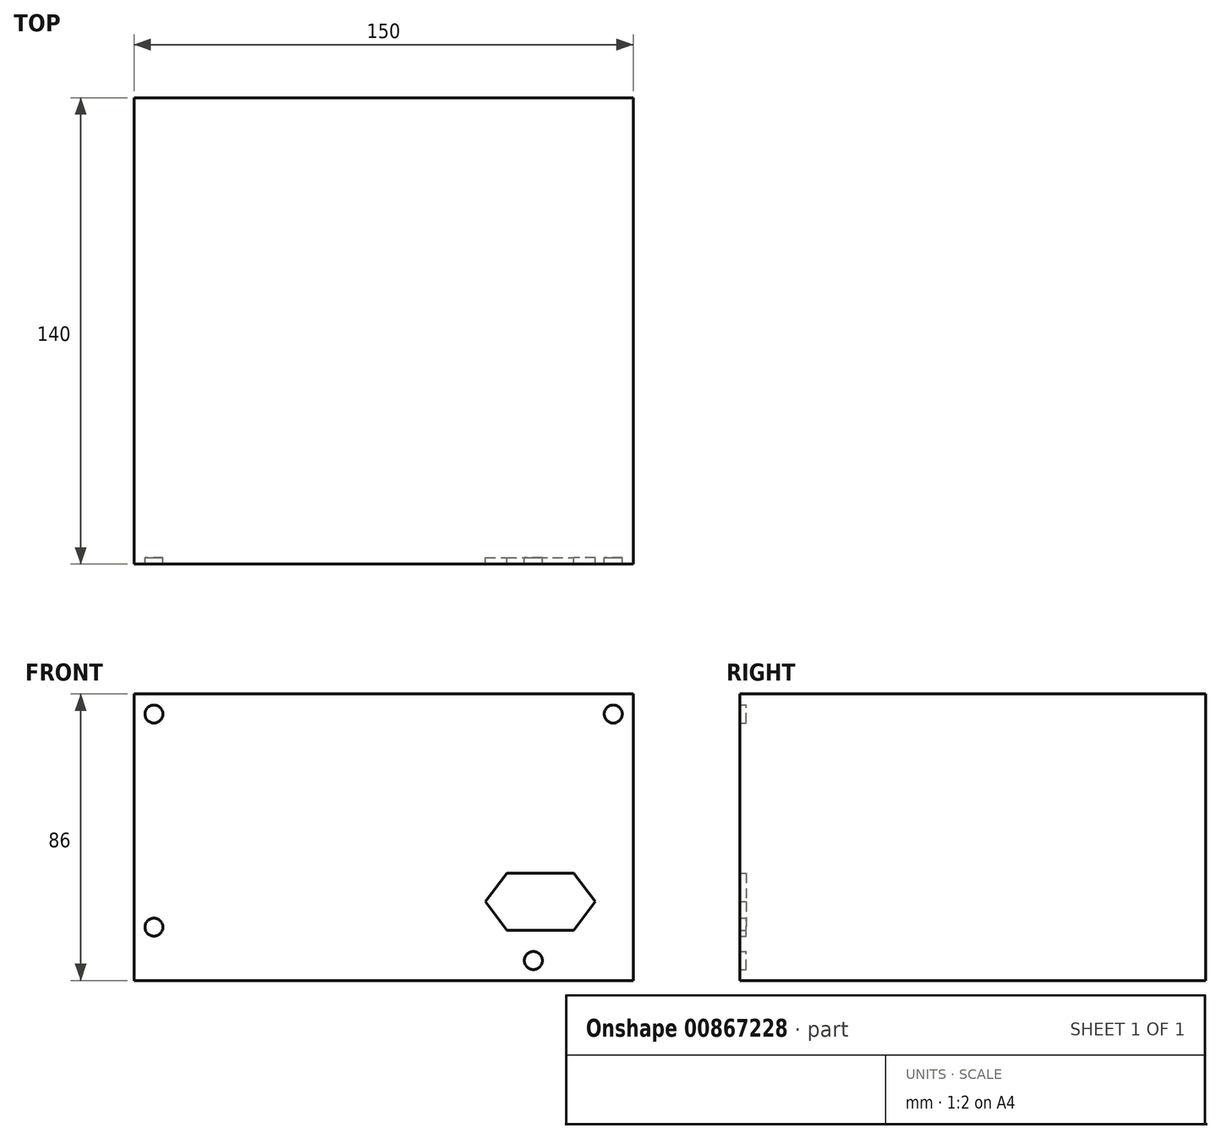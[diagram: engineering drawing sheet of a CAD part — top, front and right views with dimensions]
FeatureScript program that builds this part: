
annotation { "Feature Type Name" : "Feature", "Feature Type Description" : "" }
export const myFeature = defineFeature(function(context is Context, id is Id, definition is map)
    precondition{}
    {
        {
            var Q0;
            Q0=qCreatedBy(makeId("Front.planeOp"),FACE);
            var sketch = newSketch(context, id + "F0", { "sketchPlane" : qUnion([Q0])});
            skLineSegment(sketch, "E0.bottom", {"start": v(-61.13, 41.04) * mm, "end": v(88.87, 41.04) * mm});
            skLineSegment(sketch, "E0.top", {"start": v(-61.13, -44.96) * mm, "end": v(88.87, -44.96) * mm});
            skLineSegment(sketch, "E0.left", {"start": v(-61.13, 41.04) * mm, "end": v(-61.13, -44.96) * mm});
            skLineSegment(sketch, "E0.right", {"start": v(88.87, 41.04) * mm, "end": v(88.87, -44.96) * mm});
            skCircle(sketch, "E1", {"center": v(-55.13, 35.04) * mm, "radius": 2.7 * mm});
            skLineSegment(sketch, "E2", {"start": v(-55.13, 35.04) * mm, "end": v(-55.13, 41.04) * mm, "construction": true});
            skLineSegment(sketch, "E3", {"start": v(-55.13, 35.04) * mm, "end": v(-61.13, 35.04) * mm, "construction": true});
            skCircle(sketch, "E4", {"center": v(82.87, 35.04) * mm, "radius": 2.7 * mm});
            skLineSegment(sketch, "E5", {"start": v(82.87, 41.04) * mm, "end": v(82.87, 35.04) * mm, "construction": true});
            skLineSegment(sketch, "E6", {"start": v(88.87, 35.04) * mm, "end": v(82.87, 35.04) * mm, "construction": true});
            skCircle(sketch, "E7", {"center": v(-55.13, -28.96) * mm, "radius": 2.7 * mm});
            skLineSegment(sketch, "E8", {"start": v(-55.13, -28.96) * mm, "end": v(-55.13, 35.04) * mm, "construction": true});
            skCircle(sketch, "E9", {"center": v(58.87, -38.96) * mm, "radius": 2.7 * mm});
            skLineSegment(sketch, "E10", {"start": v(58.87, -38.96) * mm, "end": v(88.87, -38.96) * mm, "construction": true});
            skLineSegment(sketch, "E11", {"start": v(58.87, -38.96) * mm, "end": v(58.87, -44.96) * mm, "construction": true});
            skLineSegment(sketch, "E12", {"start": v(50.88, -29.92) * mm, "end": v(71, -29.92) * mm});
            skLineSegment(sketch, "E13", {"start": v(71, -29.92) * mm, "end": v(77.4, -21.3) * mm});
            skLineSegment(sketch, "E14", {"start": v(77.4, -21.3) * mm, "end": v(71, -12.7) * mm});
            skLineSegment(sketch, "E15", {"start": v(71, -12.7) * mm, "end": v(50.88, -12.7) * mm});
            skLineSegment(sketch, "E16", {"start": v(50.88, -12.7) * mm, "end": v(44.48, -21.3) * mm});
            skLineSegment(sketch, "E17", {"start": v(44.48, -21.3) * mm, "end": v(50.88, -29.92) * mm});
            skLineSegment(sketch, "E18", {"start": v(50.88, -29.92) * mm, "end": v(50.88, -12.7) * mm, "construction": true});
            skLineSegment(sketch, "E19", {"start": v(71, -12.7) * mm, "end": v(71, -29.92) * mm, "construction": true});
            skSolve(sketch);
        }
        {
            var Q0;
            Q0=makeQuery(id+"F0.imprint","IMPRINT",FACE,{"disambiguationData":[TD([[makeQuery(id+"F0.imprint","IMPRINT",EDGE,{"derivedFrom":sQuery(id+"F0.wireOp",EDGE,"E0.bottom")}),-1.0]])]});
            extrude(context, id + "F1", {"entities" : qUnion([Q0]), "depth" : 140 * mm, "offsetDistance" : 25.4 * mm});
        }
        {
            var Q0;
            Q0=makeQuery(id+"F0.imprint","IMPRINT",FACE,{"disambiguationData":[TD([[makeQuery(id+"F0.imprint","IMPRINT",EDGE,{"derivedFrom":sQuery(id+"F0.wireOp",EDGE,"E1")}),1.0]])]});
            var Q1;
            Q1=makeQuery(id+"F0.imprint","IMPRINT",FACE,{"disambiguationData":[TD([[makeQuery(id+"F0.imprint","IMPRINT",EDGE,{"derivedFrom":sQuery(id+"F0.wireOp",EDGE,"E7")}),1.0]])]});
            var Q2;
            Q2=makeQuery(id+"F0.imprint","IMPRINT",FACE,{"disambiguationData":[TD([[makeQuery(id+"F0.imprint","IMPRINT",EDGE,{"derivedFrom":sQuery(id+"F0.wireOp",EDGE,"E9")}),1.0]])]});
            var Q3;
            Q3=makeQuery(id+"F0.imprint","IMPRINT",FACE,{"disambiguationData":[TD([[makeQuery(id+"F0.imprint","IMPRINT",EDGE,{"derivedFrom":sQuery(id+"F0.wireOp",EDGE,"E12")}),1.0]])]});
            var Q4;
            Q4=makeQuery(id+"F0.imprint","IMPRINT",FACE,{"disambiguationData":[TD([[makeQuery(id+"F0.imprint","IMPRINT",EDGE,{"derivedFrom":sQuery(id+"F0.wireOp",EDGE,"E4")}),1.0]])]});
            extrude(context, id + "F2", {"entities" : qUnion([Q0, Q1, Q2, Q3, Q4]), "operationType" : NewBodyOperationType.ADD, "depth" : 138 * mm, "offsetDistance" : 25.4 * mm});
        }
    });
